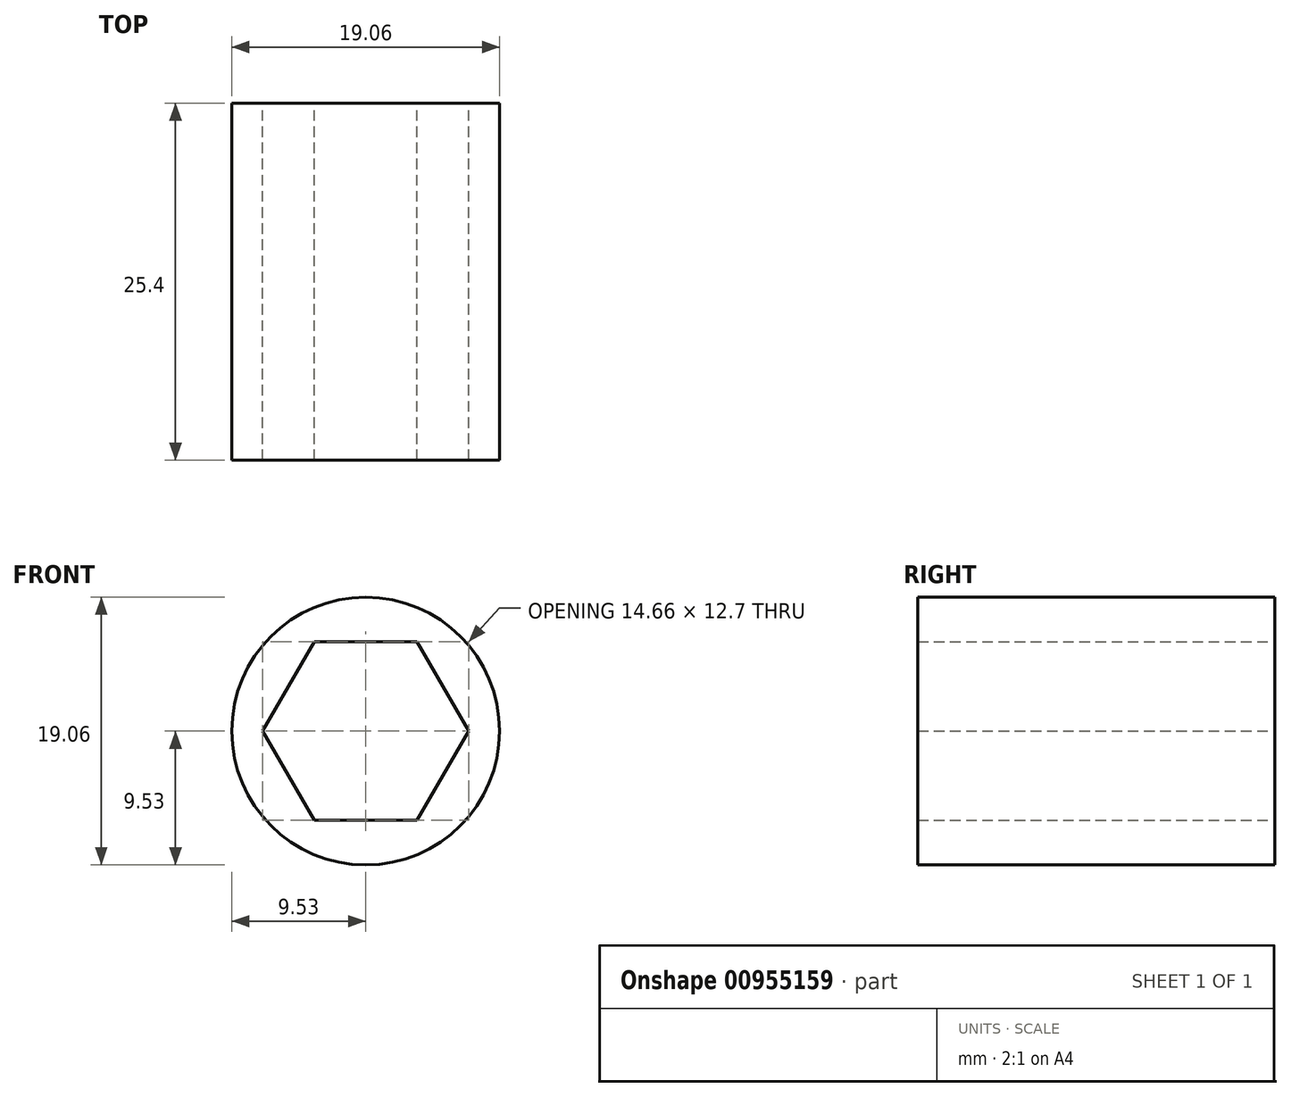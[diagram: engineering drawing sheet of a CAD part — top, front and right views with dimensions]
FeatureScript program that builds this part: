
annotation { "Feature Type Name" : "Feature", "Feature Type Description" : "" }
export const myFeature = defineFeature(function(context is Context, id is Id, definition is map)
    precondition{}
    {
        {
            var Q0;
            Q0=qCreatedBy(makeId("Front.planeOp"),FACE);
            var sketch = newSketch(context, id + "F0", { "sketchPlane" : qUnion([Q0])});
            skCircle(sketch, "E0", {"center": v(0, 0) * mm, "radius": 9.53 * mm});
            skCircle(sketch, "E1.cCircle", {"center": v(0, 0) * mm, "radius": 6.35 * mm, "construction": true});
            skLineSegment(sketch, "E1.0", {"start": v(-3.67, 6.35) * mm, "end": v(3.67, 6.35) * mm});
            skLineSegment(sketch, "E1.1", {"start": v(3.67, 6.35) * mm, "end": v(7.33, 0) * mm});
            skLineSegment(sketch, "E1.2", {"start": v(7.33, 0) * mm, "end": v(3.67, -6.35) * mm});
            skLineSegment(sketch, "E1.3", {"start": v(3.67, -6.35) * mm, "end": v(-3.67, -6.35) * mm});
            skLineSegment(sketch, "E1.4", {"start": v(-3.67, -6.35) * mm, "end": v(-7.33, 0) * mm});
            skLineSegment(sketch, "E1.5", {"start": v(-7.33, 0) * mm, "end": v(-3.67, 6.35) * mm});
            skPoint(sketch, "E1.0.midPoint", {"position": v(0, 6.35) * mm});
            skSolve(sketch);
        }
        {
            var Q0;
            Q0=qSketchRegion(id+"F0",true);
            extrude(context, id + "F1", {"entities" : qUnion([Q0]), "depth" : 25.4 * mm, "offsetDistance" : 25.4 * mm});
        }
    });
